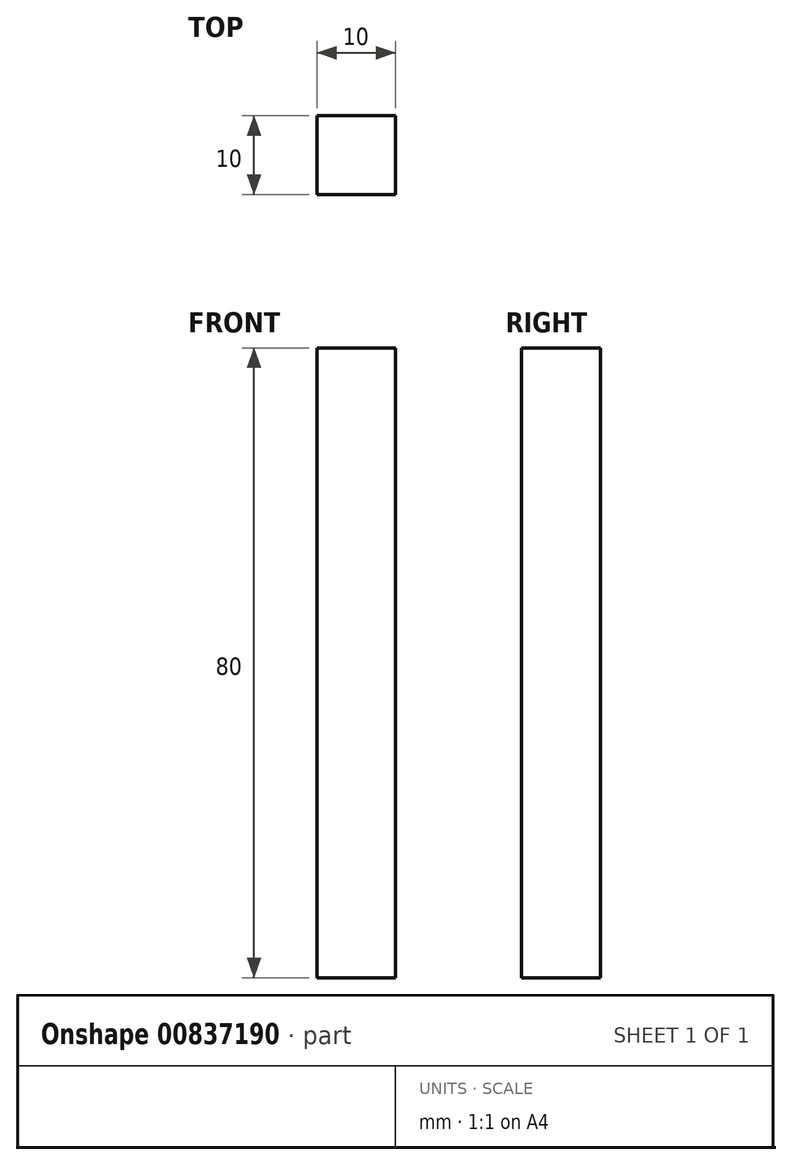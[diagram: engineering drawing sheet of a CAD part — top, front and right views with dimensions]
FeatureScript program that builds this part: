
annotation { "Feature Type Name" : "Feature", "Feature Type Description" : "" }
export const myFeature = defineFeature(function(context is Context, id is Id, definition is map)
    precondition{}
    {
        {
            assignVariable(context, id + "F0", {"name" : "length", "anyValue" : 80 * mm});
        }
        {
            var Q0;
            Q0=qCreatedBy(makeId("Top.planeOp"),FACE);
            var sketch = newSketch(context, id + "F1", { "sketchPlane" : qUnion([Q0])});
            skLineSegment(sketch, "E0.bottom", {"start": v(-50.91, -0.63) * mm, "end": v(-40.91, -0.63) * mm});
            skLineSegment(sketch, "E0.top", {"start": v(-50.91, -10.63) * mm, "end": v(-40.91, -10.63) * mm});
            skLineSegment(sketch, "E0.left", {"start": v(-50.91, -0.63) * mm, "end": v(-50.91, -10.63) * mm});
            skLineSegment(sketch, "E0.right", {"start": v(-40.91, -0.63) * mm, "end": v(-40.91, -10.63) * mm});
            skSolve(sketch);
        }
        {
            var Q0;
            Q0=makeQuery(id+"F1.imprint","IMPRINT",FACE,{"disambiguationData":[TD([[makeQuery(id+"F1.imprint","IMPRINT",EDGE,{"derivedFrom":sQuery(id+"F1.wireOp",EDGE,"E0.bottom")}),-1.0]])]});
            extrude(context, id + "F2", {"entities" : qUnion([Q0]), "depth" : getVariable(context, 'length'), "offsetDistance" : 25.4 * mm});
        }
    });
